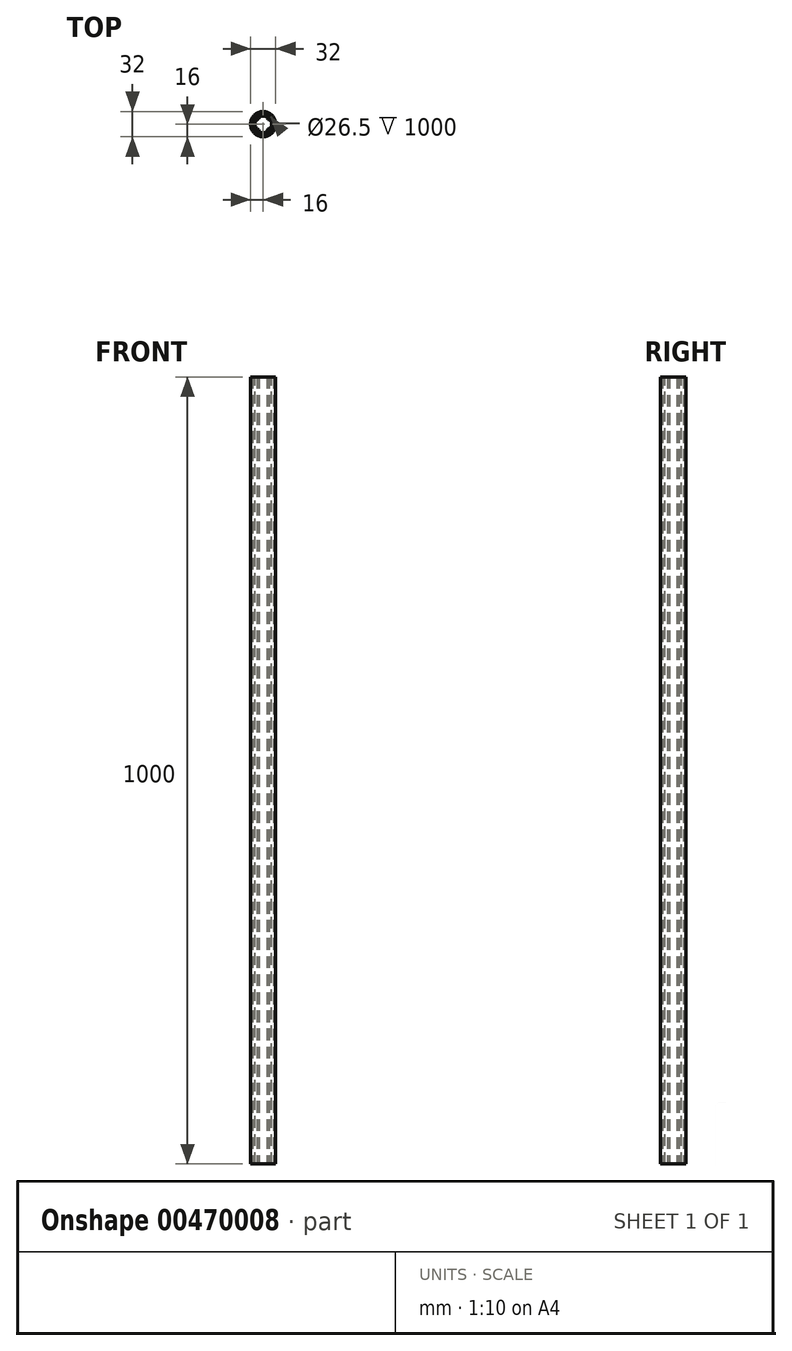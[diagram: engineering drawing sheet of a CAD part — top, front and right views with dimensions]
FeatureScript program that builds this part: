
annotation { "Feature Type Name" : "Feature", "Feature Type Description" : "" }
export const myFeature = defineFeature(function(context is Context, id is Id, definition is map)
    precondition{}
    {
        {
            var Q0;
            Q0=qCreatedBy(makeId("Top.planeOp"),FACE);
            var sketch = newSketch(context, id + "F0", { "sketchPlane" : qUnion([Q0])});
            skCircle(sketch, "E0", {"center": v(0, 0) * mm, "radius": 9 * mm});
            skSolve(sketch);
        }
        {
            var Q0;
            Q0 = qSketchRegion(id + "F0", true);
            extrude(context, id + "F1", {"entities" : qUnion([Q0]), "endBound" : BoundingType.SYMMETRIC, "depth" : 1000 * mm, "offsetDistance" : 25 * mm});
        }
        {
            var Q0;
            Q0=qCreatedBy(makeId("Front.planeOp"),FACE);
            var sketch = newSketch(context, id + "F2", { "sketchPlane" : qUnion([Q0])});
            skLineSegment(sketch, "E1.bottom", {"start": v(2.5, -489.17) * mm, "end": v(-2.5, -489.17) * mm});
            skLineSegment(sketch, "E1.top", {"start": v(2.5, -494.17) * mm, "end": v(-2.5, -494.17) * mm});
            skLineSegment(sketch, "E1.left", {"start": v(2.5, -489.17) * mm, "end": v(2.5, -494.17) * mm});
            skLineSegment(sketch, "E1.right", {"start": v(-2.5, -489.17) * mm, "end": v(-2.5, -494.17) * mm});
            skPoint(sketch, "E1.middle", {"position": v(0, -491.67) * mm});
            skLineSegment(sketch, "E2.0.1.0", {"start": v(2.5, -472.5) * mm, "end": v(-2.5, -472.5) * mm});
            skLineSegment(sketch, "E2.0.1.1", {"start": v(2.5, -472.5) * mm, "end": v(2.5, -477.5) * mm});
            skLineSegment(sketch, "E2.0.1.2", {"start": v(2.5, -477.5) * mm, "end": v(-2.5, -477.5) * mm});
            skLineSegment(sketch, "E2.0.1.3", {"start": v(-2.5, -472.5) * mm, "end": v(-2.5, -477.5) * mm});
            skLineSegment(sketch, "E2.0.2.0", {"start": v(2.5, -455.83) * mm, "end": v(-2.5, -455.83) * mm});
            skLineSegment(sketch, "E2.0.2.1", {"start": v(2.5, -455.83) * mm, "end": v(2.5, -460.83) * mm});
            skLineSegment(sketch, "E2.0.2.2", {"start": v(2.5, -460.83) * mm, "end": v(-2.5, -460.83) * mm});
            skLineSegment(sketch, "E2.0.2.3", {"start": v(-2.5, -455.83) * mm, "end": v(-2.5, -460.83) * mm});
            skLineSegment(sketch, "E2.0.3.0", {"start": v(2.5, -439.17) * mm, "end": v(-2.5, -439.17) * mm});
            skLineSegment(sketch, "E2.0.3.1", {"start": v(2.5, -439.17) * mm, "end": v(2.5, -444.17) * mm});
            skLineSegment(sketch, "E2.0.3.2", {"start": v(2.5, -444.17) * mm, "end": v(-2.5, -444.17) * mm});
            skLineSegment(sketch, "E2.0.3.3", {"start": v(-2.5, -439.17) * mm, "end": v(-2.5, -444.17) * mm});
            skLineSegment(sketch, "E2.0.4.0", {"start": v(2.5, -422.5) * mm, "end": v(-2.5, -422.5) * mm});
            skLineSegment(sketch, "E2.0.4.1", {"start": v(2.5, -422.5) * mm, "end": v(2.5, -427.5) * mm});
            skLineSegment(sketch, "E2.0.4.2", {"start": v(2.5, -427.5) * mm, "end": v(-2.5, -427.5) * mm});
            skLineSegment(sketch, "E2.0.4.3", {"start": v(-2.5, -422.5) * mm, "end": v(-2.5, -427.5) * mm});
            skLineSegment(sketch, "E2.0.5.0", {"start": v(2.5, -405.83) * mm, "end": v(-2.5, -405.83) * mm});
            skLineSegment(sketch, "E2.0.5.1", {"start": v(2.5, -405.83) * mm, "end": v(2.5, -410.83) * mm});
            skLineSegment(sketch, "E2.0.5.2", {"start": v(2.5, -410.83) * mm, "end": v(-2.5, -410.83) * mm});
            skLineSegment(sketch, "E2.0.5.3", {"start": v(-2.5, -405.83) * mm, "end": v(-2.5, -410.83) * mm});
            skLineSegment(sketch, "E2.0.6.0", {"start": v(2.5, -389.17) * mm, "end": v(-2.5, -389.17) * mm});
            skLineSegment(sketch, "E2.0.6.1", {"start": v(2.5, -389.17) * mm, "end": v(2.5, -394.17) * mm});
            skLineSegment(sketch, "E2.0.6.2", {"start": v(2.5, -394.17) * mm, "end": v(-2.5, -394.17) * mm});
            skLineSegment(sketch, "E2.0.6.3", {"start": v(-2.5, -389.17) * mm, "end": v(-2.5, -394.17) * mm});
            skLineSegment(sketch, "E2.0.7.0", {"start": v(2.5, -372.5) * mm, "end": v(-2.5, -372.5) * mm});
            skLineSegment(sketch, "E2.0.7.1", {"start": v(2.5, -372.5) * mm, "end": v(2.5, -377.5) * mm});
            skLineSegment(sketch, "E2.0.7.2", {"start": v(2.5, -377.5) * mm, "end": v(-2.5, -377.5) * mm});
            skLineSegment(sketch, "E2.0.7.3", {"start": v(-2.5, -372.5) * mm, "end": v(-2.5, -377.5) * mm});
            skLineSegment(sketch, "E2.0.8.0", {"start": v(2.5, -355.83) * mm, "end": v(-2.5, -355.83) * mm});
            skLineSegment(sketch, "E2.0.8.1", {"start": v(2.5, -355.83) * mm, "end": v(2.5, -360.83) * mm});
            skLineSegment(sketch, "E2.0.8.2", {"start": v(2.5, -360.83) * mm, "end": v(-2.5, -360.83) * mm});
            skLineSegment(sketch, "E2.0.8.3", {"start": v(-2.5, -355.83) * mm, "end": v(-2.5, -360.83) * mm});
            skLineSegment(sketch, "E2.0.9.0", {"start": v(2.5, -339.17) * mm, "end": v(-2.5, -339.17) * mm});
            skLineSegment(sketch, "E2.0.9.1", {"start": v(2.5, -339.17) * mm, "end": v(2.5, -344.17) * mm});
            skLineSegment(sketch, "E2.0.9.2", {"start": v(2.5, -344.17) * mm, "end": v(-2.5, -344.17) * mm});
            skLineSegment(sketch, "E2.0.9.3", {"start": v(-2.5, -339.17) * mm, "end": v(-2.5, -344.17) * mm});
            skLineSegment(sketch, "E2.0.10.0", {"start": v(2.5, -322.5) * mm, "end": v(-2.5, -322.5) * mm});
            skLineSegment(sketch, "E2.0.10.1", {"start": v(2.5, -322.5) * mm, "end": v(2.5, -327.5) * mm});
            skLineSegment(sketch, "E2.0.10.2", {"start": v(2.5, -327.5) * mm, "end": v(-2.5, -327.5) * mm});
            skLineSegment(sketch, "E2.0.10.3", {"start": v(-2.5, -322.5) * mm, "end": v(-2.5, -327.5) * mm});
            skLineSegment(sketch, "E2.0.11.0", {"start": v(2.5, -305.83) * mm, "end": v(-2.5, -305.83) * mm});
            skLineSegment(sketch, "E2.0.11.1", {"start": v(2.5, -305.83) * mm, "end": v(2.5, -310.83) * mm});
            skLineSegment(sketch, "E2.0.11.2", {"start": v(2.5, -310.83) * mm, "end": v(-2.5, -310.83) * mm});
            skLineSegment(sketch, "E2.0.11.3", {"start": v(-2.5, -305.83) * mm, "end": v(-2.5, -310.83) * mm});
            skLineSegment(sketch, "E2.0.12.0", {"start": v(2.5, -289.17) * mm, "end": v(-2.5, -289.17) * mm});
            skLineSegment(sketch, "E2.0.12.1", {"start": v(2.5, -289.17) * mm, "end": v(2.5, -294.17) * mm});
            skLineSegment(sketch, "E2.0.12.2", {"start": v(2.5, -294.17) * mm, "end": v(-2.5, -294.17) * mm});
            skLineSegment(sketch, "E2.0.12.3", {"start": v(-2.5, -289.17) * mm, "end": v(-2.5, -294.17) * mm});
            skLineSegment(sketch, "E2.0.13.0", {"start": v(2.5, -272.5) * mm, "end": v(-2.5, -272.5) * mm});
            skLineSegment(sketch, "E2.0.13.1", {"start": v(2.5, -272.5) * mm, "end": v(2.5, -277.5) * mm});
            skLineSegment(sketch, "E2.0.13.2", {"start": v(2.5, -277.5) * mm, "end": v(-2.5, -277.5) * mm});
            skLineSegment(sketch, "E2.0.13.3", {"start": v(-2.5, -272.5) * mm, "end": v(-2.5, -277.5) * mm});
            skLineSegment(sketch, "E2.0.14.0", {"start": v(2.5, -255.83) * mm, "end": v(-2.5, -255.83) * mm});
            skLineSegment(sketch, "E2.0.14.1", {"start": v(2.5, -255.83) * mm, "end": v(2.5, -260.83) * mm});
            skLineSegment(sketch, "E2.0.14.2", {"start": v(2.5, -260.83) * mm, "end": v(-2.5, -260.83) * mm});
            skLineSegment(sketch, "E2.0.14.3", {"start": v(-2.5, -255.83) * mm, "end": v(-2.5, -260.83) * mm});
            skLineSegment(sketch, "E2.0.15.0", {"start": v(2.5, -239.17) * mm, "end": v(-2.5, -239.17) * mm});
            skLineSegment(sketch, "E2.0.15.1", {"start": v(2.5, -239.17) * mm, "end": v(2.5, -244.17) * mm});
            skLineSegment(sketch, "E2.0.15.2", {"start": v(2.5, -244.17) * mm, "end": v(-2.5, -244.17) * mm});
            skLineSegment(sketch, "E2.0.15.3", {"start": v(-2.5, -239.17) * mm, "end": v(-2.5, -244.17) * mm});
            skLineSegment(sketch, "E2.0.16.0", {"start": v(2.5, -222.5) * mm, "end": v(-2.5, -222.5) * mm});
            skLineSegment(sketch, "E2.0.16.1", {"start": v(2.5, -222.5) * mm, "end": v(2.5, -227.5) * mm});
            skLineSegment(sketch, "E2.0.16.2", {"start": v(2.5, -227.5) * mm, "end": v(-2.5, -227.5) * mm});
            skLineSegment(sketch, "E2.0.16.3", {"start": v(-2.5, -222.5) * mm, "end": v(-2.5, -227.5) * mm});
            skLineSegment(sketch, "E2.0.17.0", {"start": v(2.5, -205.83) * mm, "end": v(-2.5, -205.83) * mm});
            skLineSegment(sketch, "E2.0.17.1", {"start": v(2.5, -205.83) * mm, "end": v(2.5, -210.83) * mm});
            skLineSegment(sketch, "E2.0.17.2", {"start": v(2.5, -210.83) * mm, "end": v(-2.5, -210.83) * mm});
            skLineSegment(sketch, "E2.0.17.3", {"start": v(-2.5, -205.83) * mm, "end": v(-2.5, -210.83) * mm});
            skLineSegment(sketch, "E2.0.18.0", {"start": v(2.5, -189.17) * mm, "end": v(-2.5, -189.17) * mm});
            skLineSegment(sketch, "E2.0.18.1", {"start": v(2.5, -189.17) * mm, "end": v(2.5, -194.17) * mm});
            skLineSegment(sketch, "E2.0.18.2", {"start": v(2.5, -194.17) * mm, "end": v(-2.5, -194.17) * mm});
            skLineSegment(sketch, "E2.0.18.3", {"start": v(-2.5, -189.17) * mm, "end": v(-2.5, -194.17) * mm});
            skLineSegment(sketch, "E2.0.19.0", {"start": v(2.5, -172.5) * mm, "end": v(-2.5, -172.5) * mm});
            skLineSegment(sketch, "E2.0.19.1", {"start": v(2.5, -172.5) * mm, "end": v(2.5, -177.5) * mm});
            skLineSegment(sketch, "E2.0.19.2", {"start": v(2.5, -177.5) * mm, "end": v(-2.5, -177.5) * mm});
            skLineSegment(sketch, "E2.0.19.3", {"start": v(-2.5, -172.5) * mm, "end": v(-2.5, -177.5) * mm});
            skLineSegment(sketch, "E2.0.20.0", {"start": v(2.5, -155.83) * mm, "end": v(-2.5, -155.83) * mm});
            skLineSegment(sketch, "E2.0.20.1", {"start": v(2.5, -155.83) * mm, "end": v(2.5, -160.83) * mm});
            skLineSegment(sketch, "E2.0.20.2", {"start": v(2.5, -160.83) * mm, "end": v(-2.5, -160.83) * mm});
            skLineSegment(sketch, "E2.0.20.3", {"start": v(-2.5, -155.83) * mm, "end": v(-2.5, -160.83) * mm});
            skLineSegment(sketch, "E2.0.21.0", {"start": v(2.5, -139.17) * mm, "end": v(-2.5, -139.17) * mm});
            skLineSegment(sketch, "E2.0.21.1", {"start": v(2.5, -139.17) * mm, "end": v(2.5, -144.17) * mm});
            skLineSegment(sketch, "E2.0.21.2", {"start": v(2.5, -144.17) * mm, "end": v(-2.5, -144.17) * mm});
            skLineSegment(sketch, "E2.0.21.3", {"start": v(-2.5, -139.17) * mm, "end": v(-2.5, -144.17) * mm});
            skLineSegment(sketch, "E2.0.22.0", {"start": v(2.5, -122.5) * mm, "end": v(-2.5, -122.5) * mm});
            skLineSegment(sketch, "E2.0.22.1", {"start": v(2.5, -122.5) * mm, "end": v(2.5, -127.5) * mm});
            skLineSegment(sketch, "E2.0.22.2", {"start": v(2.5, -127.5) * mm, "end": v(-2.5, -127.5) * mm});
            skLineSegment(sketch, "E2.0.22.3", {"start": v(-2.5, -122.5) * mm, "end": v(-2.5, -127.5) * mm});
            skLineSegment(sketch, "E2.0.23.0", {"start": v(2.5, -105.83) * mm, "end": v(-2.5, -105.83) * mm});
            skLineSegment(sketch, "E2.0.23.1", {"start": v(2.5, -105.83) * mm, "end": v(2.5, -110.83) * mm});
            skLineSegment(sketch, "E2.0.23.2", {"start": v(2.5, -110.83) * mm, "end": v(-2.5, -110.83) * mm});
            skLineSegment(sketch, "E2.0.23.3", {"start": v(-2.5, -105.83) * mm, "end": v(-2.5, -110.83) * mm});
            skLineSegment(sketch, "E2.0.24.0", {"start": v(2.5, -89.17) * mm, "end": v(-2.5, -89.17) * mm});
            skLineSegment(sketch, "E2.0.24.1", {"start": v(2.5, -89.17) * mm, "end": v(2.5, -94.17) * mm});
            skLineSegment(sketch, "E2.0.24.2", {"start": v(2.5, -94.17) * mm, "end": v(-2.5, -94.17) * mm});
            skLineSegment(sketch, "E2.0.24.3", {"start": v(-2.5, -89.17) * mm, "end": v(-2.5, -94.17) * mm});
            skLineSegment(sketch, "E2.0.25.0", {"start": v(2.5, -72.5) * mm, "end": v(-2.5, -72.5) * mm});
            skLineSegment(sketch, "E2.0.25.1", {"start": v(2.5, -72.5) * mm, "end": v(2.5, -77.5) * mm});
            skLineSegment(sketch, "E2.0.25.2", {"start": v(2.5, -77.5) * mm, "end": v(-2.5, -77.5) * mm});
            skLineSegment(sketch, "E2.0.25.3", {"start": v(-2.5, -72.5) * mm, "end": v(-2.5, -77.5) * mm});
            skLineSegment(sketch, "E2.0.26.0", {"start": v(2.5, -55.83) * mm, "end": v(-2.5, -55.83) * mm});
            skLineSegment(sketch, "E2.0.26.1", {"start": v(2.5, -55.83) * mm, "end": v(2.5, -60.83) * mm});
            skLineSegment(sketch, "E2.0.26.2", {"start": v(2.5, -60.83) * mm, "end": v(-2.5, -60.83) * mm});
            skLineSegment(sketch, "E2.0.26.3", {"start": v(-2.5, -55.83) * mm, "end": v(-2.5, -60.83) * mm});
            skLineSegment(sketch, "E2.0.27.0", {"start": v(2.5, -39.17) * mm, "end": v(-2.5, -39.17) * mm});
            skLineSegment(sketch, "E2.0.27.1", {"start": v(2.5, -39.17) * mm, "end": v(2.5, -44.17) * mm});
            skLineSegment(sketch, "E2.0.27.2", {"start": v(2.5, -44.17) * mm, "end": v(-2.5, -44.17) * mm});
            skLineSegment(sketch, "E2.0.27.3", {"start": v(-2.5, -39.17) * mm, "end": v(-2.5, -44.17) * mm});
            skLineSegment(sketch, "E2.0.28.0", {"start": v(2.5, -22.5) * mm, "end": v(-2.5, -22.5) * mm});
            skLineSegment(sketch, "E2.0.28.1", {"start": v(2.5, -22.5) * mm, "end": v(2.5, -27.5) * mm});
            skLineSegment(sketch, "E2.0.28.2", {"start": v(2.5, -27.5) * mm, "end": v(-2.5, -27.5) * mm});
            skLineSegment(sketch, "E2.0.28.3", {"start": v(-2.5, -22.5) * mm, "end": v(-2.5, -27.5) * mm});
            skLineSegment(sketch, "E2.0.29.0", {"start": v(2.5, -5.83) * mm, "end": v(-2.5, -5.83) * mm});
            skLineSegment(sketch, "E2.0.29.1", {"start": v(2.5, -5.83) * mm, "end": v(2.5, -10.83) * mm});
            skLineSegment(sketch, "E2.0.29.2", {"start": v(2.5, -10.83) * mm, "end": v(-2.5, -10.83) * mm});
            skLineSegment(sketch, "E2.0.29.3", {"start": v(-2.5, -5.83) * mm, "end": v(-2.5, -10.83) * mm});
            skLineSegment(sketch, "E2.0.30.0", {"start": v(2.5, 10.83) * mm, "end": v(-2.5, 10.83) * mm});
            skLineSegment(sketch, "E2.0.30.1", {"start": v(2.5, 10.83) * mm, "end": v(2.5, 5.83) * mm});
            skLineSegment(sketch, "E2.0.30.2", {"start": v(2.5, 5.83) * mm, "end": v(-2.5, 5.83) * mm});
            skLineSegment(sketch, "E2.0.30.3", {"start": v(-2.5, 10.83) * mm, "end": v(-2.5, 5.83) * mm});
            skLineSegment(sketch, "E2.0.31.0", {"start": v(2.5, 27.5) * mm, "end": v(-2.5, 27.5) * mm});
            skLineSegment(sketch, "E2.0.31.1", {"start": v(2.5, 27.5) * mm, "end": v(2.5, 22.5) * mm});
            skLineSegment(sketch, "E2.0.31.2", {"start": v(2.5, 22.5) * mm, "end": v(-2.5, 22.5) * mm});
            skLineSegment(sketch, "E2.0.31.3", {"start": v(-2.5, 27.5) * mm, "end": v(-2.5, 22.5) * mm});
            skLineSegment(sketch, "E2.0.32.0", {"start": v(2.5, 44.17) * mm, "end": v(-2.5, 44.17) * mm});
            skLineSegment(sketch, "E2.0.32.1", {"start": v(2.5, 44.17) * mm, "end": v(2.5, 39.17) * mm});
            skLineSegment(sketch, "E2.0.32.2", {"start": v(2.5, 39.17) * mm, "end": v(-2.5, 39.17) * mm});
            skLineSegment(sketch, "E2.0.32.3", {"start": v(-2.5, 44.17) * mm, "end": v(-2.5, 39.17) * mm});
            skLineSegment(sketch, "E2.0.33.0", {"start": v(2.5, 60.83) * mm, "end": v(-2.5, 60.83) * mm});
            skLineSegment(sketch, "E2.0.33.1", {"start": v(2.5, 60.83) * mm, "end": v(2.5, 55.83) * mm});
            skLineSegment(sketch, "E2.0.33.2", {"start": v(2.5, 55.83) * mm, "end": v(-2.5, 55.83) * mm});
            skLineSegment(sketch, "E2.0.33.3", {"start": v(-2.5, 60.83) * mm, "end": v(-2.5, 55.83) * mm});
            skLineSegment(sketch, "E2.0.34.0", {"start": v(2.5, 77.5) * mm, "end": v(-2.5, 77.5) * mm});
            skLineSegment(sketch, "E2.0.34.1", {"start": v(2.5, 77.5) * mm, "end": v(2.5, 72.5) * mm});
            skLineSegment(sketch, "E2.0.34.2", {"start": v(2.5, 72.5) * mm, "end": v(-2.5, 72.5) * mm});
            skLineSegment(sketch, "E2.0.34.3", {"start": v(-2.5, 77.5) * mm, "end": v(-2.5, 72.5) * mm});
            skLineSegment(sketch, "E2.0.35.0", {"start": v(2.5, 94.17) * mm, "end": v(-2.5, 94.17) * mm});
            skLineSegment(sketch, "E2.0.35.1", {"start": v(2.5, 94.17) * mm, "end": v(2.5, 89.17) * mm});
            skLineSegment(sketch, "E2.0.35.2", {"start": v(2.5, 89.17) * mm, "end": v(-2.5, 89.17) * mm});
            skLineSegment(sketch, "E2.0.35.3", {"start": v(-2.5, 94.17) * mm, "end": v(-2.5, 89.17) * mm});
            skLineSegment(sketch, "E2.0.36.0", {"start": v(2.5, 110.83) * mm, "end": v(-2.5, 110.83) * mm});
            skLineSegment(sketch, "E2.0.36.1", {"start": v(2.5, 110.83) * mm, "end": v(2.5, 105.83) * mm});
            skLineSegment(sketch, "E2.0.36.2", {"start": v(2.5, 105.83) * mm, "end": v(-2.5, 105.83) * mm});
            skLineSegment(sketch, "E2.0.36.3", {"start": v(-2.5, 110.83) * mm, "end": v(-2.5, 105.83) * mm});
            skLineSegment(sketch, "E2.0.37.0", {"start": v(2.5, 127.5) * mm, "end": v(-2.5, 127.5) * mm});
            skLineSegment(sketch, "E2.0.37.1", {"start": v(2.5, 127.5) * mm, "end": v(2.5, 122.5) * mm});
            skLineSegment(sketch, "E2.0.37.2", {"start": v(2.5, 122.5) * mm, "end": v(-2.5, 122.5) * mm});
            skLineSegment(sketch, "E2.0.37.3", {"start": v(-2.5, 127.5) * mm, "end": v(-2.5, 122.5) * mm});
            skLineSegment(sketch, "E2.0.38.0", {"start": v(2.5, 144.17) * mm, "end": v(-2.5, 144.17) * mm});
            skLineSegment(sketch, "E2.0.38.1", {"start": v(2.5, 144.17) * mm, "end": v(2.5, 139.17) * mm});
            skLineSegment(sketch, "E2.0.38.2", {"start": v(2.5, 139.17) * mm, "end": v(-2.5, 139.17) * mm});
            skLineSegment(sketch, "E2.0.38.3", {"start": v(-2.5, 144.17) * mm, "end": v(-2.5, 139.17) * mm});
            skLineSegment(sketch, "E2.0.39.0", {"start": v(2.5, 160.83) * mm, "end": v(-2.5, 160.83) * mm});
            skLineSegment(sketch, "E2.0.39.1", {"start": v(2.5, 160.83) * mm, "end": v(2.5, 155.83) * mm});
            skLineSegment(sketch, "E2.0.39.2", {"start": v(2.5, 155.83) * mm, "end": v(-2.5, 155.83) * mm});
            skLineSegment(sketch, "E2.0.39.3", {"start": v(-2.5, 160.83) * mm, "end": v(-2.5, 155.83) * mm});
            skLineSegment(sketch, "E2.0.40.0", {"start": v(2.5, 177.5) * mm, "end": v(-2.5, 177.5) * mm});
            skLineSegment(sketch, "E2.0.40.1", {"start": v(2.5, 177.5) * mm, "end": v(2.5, 172.5) * mm});
            skLineSegment(sketch, "E2.0.40.2", {"start": v(2.5, 172.5) * mm, "end": v(-2.5, 172.5) * mm});
            skLineSegment(sketch, "E2.0.40.3", {"start": v(-2.5, 177.5) * mm, "end": v(-2.5, 172.5) * mm});
            skLineSegment(sketch, "E2.0.41.0", {"start": v(2.5, 194.17) * mm, "end": v(-2.5, 194.17) * mm});
            skLineSegment(sketch, "E2.0.41.1", {"start": v(2.5, 194.17) * mm, "end": v(2.5, 189.17) * mm});
            skLineSegment(sketch, "E2.0.41.2", {"start": v(2.5, 189.17) * mm, "end": v(-2.5, 189.17) * mm});
            skLineSegment(sketch, "E2.0.41.3", {"start": v(-2.5, 194.17) * mm, "end": v(-2.5, 189.17) * mm});
            skLineSegment(sketch, "E2.0.42.0", {"start": v(2.5, 210.83) * mm, "end": v(-2.5, 210.83) * mm});
            skLineSegment(sketch, "E2.0.42.1", {"start": v(2.5, 210.83) * mm, "end": v(2.5, 205.83) * mm});
            skLineSegment(sketch, "E2.0.42.2", {"start": v(2.5, 205.83) * mm, "end": v(-2.5, 205.83) * mm});
            skLineSegment(sketch, "E2.0.42.3", {"start": v(-2.5, 210.83) * mm, "end": v(-2.5, 205.83) * mm});
            skLineSegment(sketch, "E2.0.43.0", {"start": v(2.5, 227.5) * mm, "end": v(-2.5, 227.5) * mm});
            skLineSegment(sketch, "E2.0.43.1", {"start": v(2.5, 227.5) * mm, "end": v(2.5, 222.5) * mm});
            skLineSegment(sketch, "E2.0.43.2", {"start": v(2.5, 222.5) * mm, "end": v(-2.5, 222.5) * mm});
            skLineSegment(sketch, "E2.0.43.3", {"start": v(-2.5, 227.5) * mm, "end": v(-2.5, 222.5) * mm});
            skLineSegment(sketch, "E2.0.44.0", {"start": v(2.5, 244.17) * mm, "end": v(-2.5, 244.17) * mm});
            skLineSegment(sketch, "E2.0.44.1", {"start": v(2.5, 244.17) * mm, "end": v(2.5, 239.17) * mm});
            skLineSegment(sketch, "E2.0.44.2", {"start": v(2.5, 239.17) * mm, "end": v(-2.5, 239.17) * mm});
            skLineSegment(sketch, "E2.0.44.3", {"start": v(-2.5, 244.17) * mm, "end": v(-2.5, 239.17) * mm});
            skLineSegment(sketch, "E2.0.45.0", {"start": v(2.5, 260.83) * mm, "end": v(-2.5, 260.83) * mm});
            skLineSegment(sketch, "E2.0.45.1", {"start": v(2.5, 260.83) * mm, "end": v(2.5, 255.83) * mm});
            skLineSegment(sketch, "E2.0.45.2", {"start": v(2.5, 255.83) * mm, "end": v(-2.5, 255.83) * mm});
            skLineSegment(sketch, "E2.0.45.3", {"start": v(-2.5, 260.83) * mm, "end": v(-2.5, 255.83) * mm});
            skLineSegment(sketch, "E2.0.46.0", {"start": v(2.5, 277.5) * mm, "end": v(-2.5, 277.5) * mm});
            skLineSegment(sketch, "E2.0.46.1", {"start": v(2.5, 277.5) * mm, "end": v(2.5, 272.5) * mm});
            skLineSegment(sketch, "E2.0.46.2", {"start": v(2.5, 272.5) * mm, "end": v(-2.5, 272.5) * mm});
            skLineSegment(sketch, "E2.0.46.3", {"start": v(-2.5, 277.5) * mm, "end": v(-2.5, 272.5) * mm});
            skLineSegment(sketch, "E2.0.47.0", {"start": v(2.5, 294.17) * mm, "end": v(-2.5, 294.17) * mm});
            skLineSegment(sketch, "E2.0.47.1", {"start": v(2.5, 294.17) * mm, "end": v(2.5, 289.17) * mm});
            skLineSegment(sketch, "E2.0.47.2", {"start": v(2.5, 289.17) * mm, "end": v(-2.5, 289.17) * mm});
            skLineSegment(sketch, "E2.0.47.3", {"start": v(-2.5, 294.17) * mm, "end": v(-2.5, 289.17) * mm});
            skLineSegment(sketch, "E2.0.48.0", {"start": v(2.5, 310.83) * mm, "end": v(-2.5, 310.83) * mm});
            skLineSegment(sketch, "E2.0.48.1", {"start": v(2.5, 310.83) * mm, "end": v(2.5, 305.83) * mm});
            skLineSegment(sketch, "E2.0.48.2", {"start": v(2.5, 305.83) * mm, "end": v(-2.5, 305.83) * mm});
            skLineSegment(sketch, "E2.0.48.3", {"start": v(-2.5, 310.83) * mm, "end": v(-2.5, 305.83) * mm});
            skLineSegment(sketch, "E2.0.49.0", {"start": v(2.5, 327.5) * mm, "end": v(-2.5, 327.5) * mm});
            skLineSegment(sketch, "E2.0.49.1", {"start": v(2.5, 327.5) * mm, "end": v(2.5, 322.5) * mm});
            skLineSegment(sketch, "E2.0.49.2", {"start": v(2.5, 322.5) * mm, "end": v(-2.5, 322.5) * mm});
            skLineSegment(sketch, "E2.0.49.3", {"start": v(-2.5, 327.5) * mm, "end": v(-2.5, 322.5) * mm});
            skLineSegment(sketch, "E2.0.50.0", {"start": v(2.5, 344.17) * mm, "end": v(-2.5, 344.17) * mm});
            skLineSegment(sketch, "E2.0.50.1", {"start": v(2.5, 344.17) * mm, "end": v(2.5, 339.17) * mm});
            skLineSegment(sketch, "E2.0.50.2", {"start": v(2.5, 339.17) * mm, "end": v(-2.5, 339.17) * mm});
            skLineSegment(sketch, "E2.0.50.3", {"start": v(-2.5, 344.17) * mm, "end": v(-2.5, 339.17) * mm});
            skLineSegment(sketch, "E2.0.51.0", {"start": v(2.5, 360.83) * mm, "end": v(-2.5, 360.83) * mm});
            skLineSegment(sketch, "E2.0.51.1", {"start": v(2.5, 360.83) * mm, "end": v(2.5, 355.83) * mm});
            skLineSegment(sketch, "E2.0.51.2", {"start": v(2.5, 355.83) * mm, "end": v(-2.5, 355.83) * mm});
            skLineSegment(sketch, "E2.0.51.3", {"start": v(-2.5, 360.83) * mm, "end": v(-2.5, 355.83) * mm});
            skLineSegment(sketch, "E2.0.52.0", {"start": v(2.5, 377.5) * mm, "end": v(-2.5, 377.5) * mm});
            skLineSegment(sketch, "E2.0.52.1", {"start": v(2.5, 377.5) * mm, "end": v(2.5, 372.5) * mm});
            skLineSegment(sketch, "E2.0.52.2", {"start": v(2.5, 372.5) * mm, "end": v(-2.5, 372.5) * mm});
            skLineSegment(sketch, "E2.0.52.3", {"start": v(-2.5, 377.5) * mm, "end": v(-2.5, 372.5) * mm});
            skLineSegment(sketch, "E2.0.53.0", {"start": v(2.5, 394.17) * mm, "end": v(-2.5, 394.17) * mm});
            skLineSegment(sketch, "E2.0.53.1", {"start": v(2.5, 394.17) * mm, "end": v(2.5, 389.17) * mm});
            skLineSegment(sketch, "E2.0.53.2", {"start": v(2.5, 389.17) * mm, "end": v(-2.5, 389.17) * mm});
            skLineSegment(sketch, "E2.0.53.3", {"start": v(-2.5, 394.17) * mm, "end": v(-2.5, 389.17) * mm});
            skLineSegment(sketch, "E2.0.54.0", {"start": v(2.5, 410.83) * mm, "end": v(-2.5, 410.83) * mm});
            skLineSegment(sketch, "E2.0.54.1", {"start": v(2.5, 410.83) * mm, "end": v(2.5, 405.83) * mm});
            skLineSegment(sketch, "E2.0.54.2", {"start": v(2.5, 405.83) * mm, "end": v(-2.5, 405.83) * mm});
            skLineSegment(sketch, "E2.0.54.3", {"start": v(-2.5, 410.83) * mm, "end": v(-2.5, 405.83) * mm});
            skLineSegment(sketch, "E2.0.55.0", {"start": v(2.5, 427.5) * mm, "end": v(-2.5, 427.5) * mm});
            skLineSegment(sketch, "E2.0.55.1", {"start": v(2.5, 427.5) * mm, "end": v(2.5, 422.5) * mm});
            skLineSegment(sketch, "E2.0.55.2", {"start": v(2.5, 422.5) * mm, "end": v(-2.5, 422.5) * mm});
            skLineSegment(sketch, "E2.0.55.3", {"start": v(-2.5, 427.5) * mm, "end": v(-2.5, 422.5) * mm});
            skLineSegment(sketch, "E2.0.56.0", {"start": v(2.5, 444.17) * mm, "end": v(-2.5, 444.17) * mm});
            skLineSegment(sketch, "E2.0.56.1", {"start": v(2.5, 444.17) * mm, "end": v(2.5, 439.17) * mm});
            skLineSegment(sketch, "E2.0.56.2", {"start": v(2.5, 439.17) * mm, "end": v(-2.5, 439.17) * mm});
            skLineSegment(sketch, "E2.0.56.3", {"start": v(-2.5, 444.17) * mm, "end": v(-2.5, 439.17) * mm});
            skLineSegment(sketch, "E2.0.57.0", {"start": v(2.5, 460.83) * mm, "end": v(-2.5, 460.83) * mm});
            skLineSegment(sketch, "E2.0.57.1", {"start": v(2.5, 460.83) * mm, "end": v(2.5, 455.83) * mm});
            skLineSegment(sketch, "E2.0.57.2", {"start": v(2.5, 455.83) * mm, "end": v(-2.5, 455.83) * mm});
            skLineSegment(sketch, "E2.0.57.3", {"start": v(-2.5, 460.83) * mm, "end": v(-2.5, 455.83) * mm});
            skLineSegment(sketch, "E2.0.58.0", {"start": v(2.5, 477.5) * mm, "end": v(-2.5, 477.5) * mm});
            skLineSegment(sketch, "E2.0.58.1", {"start": v(2.5, 477.5) * mm, "end": v(2.5, 472.5) * mm});
            skLineSegment(sketch, "E2.0.58.2", {"start": v(2.5, 472.5) * mm, "end": v(-2.5, 472.5) * mm});
            skLineSegment(sketch, "E2.0.58.3", {"start": v(-2.5, 477.5) * mm, "end": v(-2.5, 472.5) * mm});
            skLineSegment(sketch, "E2.0.59.0", {"start": v(2.5, 494.17) * mm, "end": v(-2.5, 494.17) * mm});
            skLineSegment(sketch, "E2.0.59.1", {"start": v(2.5, 494.17) * mm, "end": v(2.5, 489.17) * mm});
            skLineSegment(sketch, "E2.0.59.2", {"start": v(2.5, 489.17) * mm, "end": v(-2.5, 489.17) * mm});
            skLineSegment(sketch, "E2.0.59.3", {"start": v(-2.5, 494.17) * mm, "end": v(-2.5, 489.17) * mm});
            skLineSegment(sketch, "E2.direction1", {"start": v(-2.5, -489.17) * mm, "end": v(22.5, -489.17) * mm, "construction": true});
            skLineSegment(sketch, "E2.direction2", {"start": v(-2.5, -489.17) * mm, "end": v(-2.5, -472.5) * mm, "construction": true});
            skSolve(sketch);
        }
        {
            var Q0;
            Q0=qCreatedBy(makeId("Right.planeOp"),FACE);
            var sketch = newSketch(context, id + "F3", { "sketchPlane" : qUnion([Q0])});
            skLineSegment(sketch, "E3.bottom", {"start": v(-5, -500) * mm, "end": v(5, -500) * mm});
            skLineSegment(sketch, "E3.top", {"start": v(-5, 500) * mm, "end": v(5, 500) * mm});
            skLineSegment(sketch, "E3.left", {"start": v(-5, -500) * mm, "end": v(-5, 500) * mm});
            skLineSegment(sketch, "E3.right", {"start": v(5, -500) * mm, "end": v(5, 500) * mm});
            skPoint(sketch, "E3.middle", {"position": v(0, 0) * mm});
            skSolve(sketch);
        }
        {
            var Q0;
            Q0 = qSketchRegion(id + "F3", true);
            extrude(context, id + "F4", {"entities" : qUnion([Q0]), "operationType" : NewBodyOperationType.ADD, "endBound" : BoundingType.SYMMETRIC, "depth" : 21 * mm, "offsetDistance" : 25 * mm});
        }
        {
            var Q0;
            Q0=qCreatedBy(makeId("Front.planeOp"),FACE);
            var sketch = newSketch(context, id + "F5", { "sketchPlane" : qUnion([Q0])});
            skLineSegment(sketch, "E4.bottom", {"start": v(-5, -500) * mm, "end": v(5, -500) * mm});
            skLineSegment(sketch, "E4.top", {"start": v(-5, 500) * mm, "end": v(5, 500) * mm});
            skLineSegment(sketch, "E4.left", {"start": v(-5, -500) * mm, "end": v(-5, 500) * mm});
            skLineSegment(sketch, "E4.right", {"start": v(5, -500) * mm, "end": v(5, 500) * mm});
            skPoint(sketch, "E4.middle", {"position": v(0, 0) * mm});
            skSolve(sketch);
        }
        {
            var Q0;
            Q0 = qSketchRegion(id + "F5", true);
            extrude(context, id + "F6", {"entities" : qUnion([Q0]), "operationType" : NewBodyOperationType.ADD, "endBound" : BoundingType.SYMMETRIC, "depth" : 21 * mm, "offsetDistance" : 25 * mm});
        }
        {
            var Q0;
            Q0=qCreatedBy(makeId("Top.planeOp"),FACE);
            var sketch = newSketch(context, id + "F7", { "sketchPlane" : qUnion([Q0])});
            skCircle(sketch, "E5", {"center": v(0, 0) * mm, "radius": 13.25 * mm});
            skCircle(sketch, "E6", {"center": v(0, 0) * mm, "radius": 16 * mm});
            skSolve(sketch);
        }
        {
            var Q0;
            Q0 = qSketchRegion(id + "F7", true);
            extrude(context, id + "F8", {"entities" : qUnion([Q0]), "endBound" : BoundingType.SYMMETRIC, "depth" : 1000 * mm, "offsetDistance" : 25 * mm});
        }
        {
            var Q0;
            Q0=makeQuery(id+"F1.opExtrude","SWEPT_BODY",BODY,{"disambiguationData":[OSD([sQuery(id+"F0.wireOp",EDGE,"E0")])]});
            transform(context, id + "F9", {"entities" : qUnion([Q0]), "transformType" : TransformType.TRANSLATION_3D, "dx" : 57 * mm, "dy" : 0 * mm, "dz" : 0 * mm, "makeCopy" : true});
        }
        {
            var Q0;
            Q0=makeQuery(id+"F9.opPattern","COPY",BODY,{"derivedFrom":makeQuery(id+"F1.opExtrude","SWEPT_BODY",BODY,{"disambiguationData":[OSD([sQuery(id+"F0.wireOp",EDGE,"E0")])]}),"instanceName":"1"});
            deleteBodies(context, id + "F10", {"entities" : qUnion([Q0])});
        }
    });
